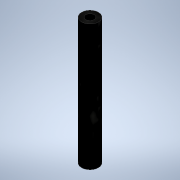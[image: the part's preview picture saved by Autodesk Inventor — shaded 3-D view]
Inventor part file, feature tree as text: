
AUTODESK INVENTOR PART (.ipt)
format: ipt  version: 2020.2 (Build 242310000, 310)  size: 96,768 bytes
history: native  units: mm
features: other x3, sketch x3, extrude x2
ambient origin geometry x8: Origin, YZ Plane, XZ Plane, XY Plane, X Axis, Y Axis, Z Axis, Center Point
bodies: Body1 (feature_tree)
feature tree (8):
  other  "ソリッド1"
  extrude  "押し出し1"  Depth=6.0mm
  other  "作業平面1"
  sketch  "スケッチ2"
  extrude  "押し出し2"  Depth=3.0mm
  sketch  "スケッチ1"
  sketch  "スケッチ3"
  other  "断面エッジを投影1"
